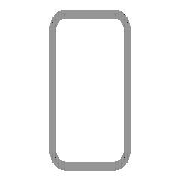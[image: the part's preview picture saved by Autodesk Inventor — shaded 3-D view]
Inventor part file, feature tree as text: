
AUTODESK INVENTOR PART (.ipt)
format: ipt  version: 2025 (Build 290162010, 162A)  size: 133,120 bytes
history: native  units: mm (DEFAULTED — no unit token found)
features: other x4, sketch x1, plane x1
ambient origin geometry x8: Origin, YZ Plane, XZ Plane, XY Plane, X Axis, Y Axis, Z Axis, Center Point
bodies: Solid1 (feature_tree), Body (feature_tree)
feature tree (6):
  parser-record x1  (decoder bookkeeping rows leaked as tree rows — omitted from the tree; the rows remain in map.json)
  other  "Driven Length"
  other  "Start Plane"
  other  "End Plane"
  sketch  "Sketch3"  dims[d3=500.0mm d4=0.0mm d7=8.0mm d9=50.0mm d11=100.0mm d12=4.0mm d13=-0.0mm d14=500.0mm d15=25.0mm d16=50.0mm d17=90.0deg d18=500.0mm]
  plane  "Work Plane3"
